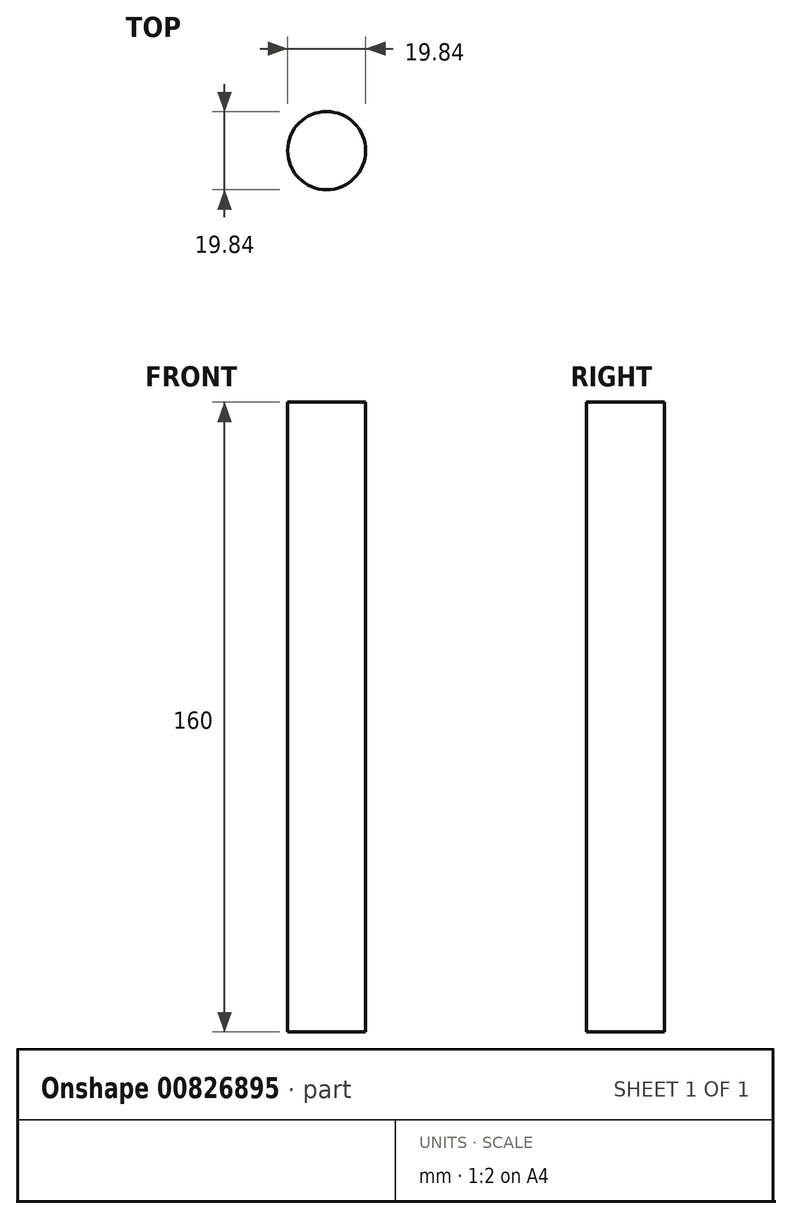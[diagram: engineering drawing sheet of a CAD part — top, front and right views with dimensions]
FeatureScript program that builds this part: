
annotation { "Feature Type Name" : "Feature", "Feature Type Description" : "" }
export const myFeature = defineFeature(function(context is Context, id is Id, definition is map)
    precondition{}
    {
        {
            var Q0;
            Q0=qCreatedBy(makeId("Top.planeOp"),FACE);
            var sketch = newSketch(context, id + "F0", { "sketchPlane" : qUnion([Q0])});
            skCircle(sketch, "E0", {"center": v(0, 0) * mm, "radius": 9.92 * mm});
            skSolve(sketch);
        }
        {
            var Q0;
            Q0=makeQuery(id+"F0.imprint","IMPRINT",FACE,{"disambiguationData":[TD([[makeQuery(id+"F0.imprint","IMPRINT",EDGE,{"derivedFrom":sQuery(id+"F0.wireOp",EDGE,"E0")}),1.0]])]});
            extrude(context, id + "F1", {"entities" : qUnion([Q0]), "depth" : 160 * mm, "offsetDistance" : 25 * mm});
        }
    });
